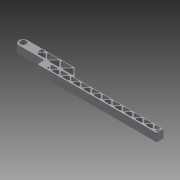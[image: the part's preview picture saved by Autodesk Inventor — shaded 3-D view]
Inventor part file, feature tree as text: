
AUTODESK INVENTOR PART (.ipt)
format: ipt  version: 2011 SP2 (Build 150309200, 309)  size: 970,752 bytes
history: native  units: mm
features: fillet x13, extrude x9, projected_geometry x8, sketch x7, plane x1, mirror x1
ambient origin geometry x8: Origin, YZ Plane, XZ Plane, XY Plane, X Axis, Y Axis, Z Axis, Center Point
feature tree (39):
  sketch  "Sketch1"  dims[d14=1.0mm d16=1.0mm]
  extrude  "Extrusion11"  Depth=1.0mm
  extrude  "Extrusion12"  Depth=1.0mm
  extrude  "Extrusion13"  Depth=16.580628mm
  extrude  "Extrusion14"  Depth=0.5mm
  extrude  "Extrusion15"  Depth=0.5mm
  extrude  "Extrusion16"  Depth=0.5mm
  fillet  "Fillet13"  Radius=0.5mm
  fillet  "Fillet14"  Radius=0.5mm
  fillet  "Fillet15"  Radius=0.5mm
  fillet  "Fillet16"  Radius=0.5mm
  fillet  "Fillet17"  Radius=0.5mm
  fillet  "Fillet18"  Radius=0.5mm
  fillet  "Fillet19"  Radius=0.5mm
  fillet  "Fillet20"  Radius=0.5mm
  fillet  "Fillet21"  Radius=0.5mm
  fillet  "Fillet22"  Radius=0.5mm
  fillet  "Fillet25"  Radius=0.5mm
  extrude  "Extrusion17"  Depth=0.5mm
  fillet  "Fillet26"  Radius=0.5mm
  extrude  "Extrusion18"  Depth=0.5mm
  fillet  "Fillet27"  Radius=0.5mm
  plane  "Work Plane2"
  mirror  "Mirror2"
  extrude  "Extrusion19"  Depth=0.5mm
  sketch  "Sketch11"  dims[d23=1.0mm d24=1.0mm]
  projected_geometry  "Projected Loop7"
  sketch  "Sketch12"  dims[d25=1.0mm d30=16.580628mm]
  projected_geometry  "Projected Loop8"
  projected_geometry  "Projected Loop9"
  sketch  "Sketch13"  dims[d32=1.0mm d62=0.5mm]
  sketch  "Sketch14"  dims[d64=0.5mm d65=0.5mm]
  sketch  "Sketch15"  dims[d66=0.5mm d68=0.5mm d69=0.5mm d70=0.5mm d71=0.5mm d72=0.5mm d73=0.5mm d74=0.5mm d75=0.5mm d76=0.5mm d77=0.5mm d78=0.5mm d79=0.5mm]
  projected_geometry  "Projected Loop10"
  projected_geometry  "Projected Loop11"
  projected_geometry  "Projected Loop12"
  projected_geometry  "Projected Loop13"
  projected_geometry  "Projected Loop14"
  sketch  "Sketch16"  dims[d80=0.5mm d81=0.5mm d82=0.5mm d83=0.5mm d84=0.5mm d85=0.5mm d86=0.5mm d87=0.5mm d88=0.5mm d89=0.5mm d90=0.5mm d91=0.5mm d92=0.5mm d93=0.5mm d94=0.5mm d95=0.5mm d96=0.5mm d97=0.5mm d98=0.5mm d99=0.5mm d100=0.5mm d101=0.5mm d102=0.5mm d103=0.5mm d104=0.5mm d106=0.5mm d107=0.5mm d108=0.5mm d109=0.5mm d115=14.209mm d116=3.912mm d120=5.45mm d121=3.75mm d122=1.875mm d124=2.725mm d126=3.060539mm d166=1.0mm d167=0.5mm d169=0.5mm d171=0.5mm d172=0.5mm d173=0.5mm d174=0.5mm d175=0.5mm d176=0.5mm d177=0.5mm d178=0.5mm d179=0.5mm d180=0.5mm d181=0.5mm d182=0.5mm d183=13.0mm d184=5.0mm d185=10.0mm d186=3.45mm d187=1.956mm d188=28.816511mm d189=34.516421mm d190=9.0mm d191=1.0mm d192=172.0mm d193=35.152794mm d194=10.0mm d195=0.0mm d196=10.0mm d197=0.0mm d198=6.85mm d199=0.0mm d200=10.0mm d201=8.0mm d202=0.0mm d203=14.835299mm d204=10.0mm d205=0.0mm d206=16.580628mm d207=10.0mm d208=0.0mm d209=1.0mm d210=1.0mm d211=0.5mm d212=1.75mm d213=0.2mm d214=1.0mm d215=0.5mm d216=0.5mm d217=0.5mm d218=1.0mm d221=2.25mm d222=10.0mm d223=0.0mm d224=0.75mm d225=10.0mm d226=0.0mm d227=0.5mm d228=-175.0mm d229=11.0mm d230=1.0mm d231=0.0mm d232=0.0mm]
